# Revit family: Cabinet_Base-Cabinet_45-Degree-With-Overhead-Countertop_Moduline
name_source: partatom
category: Furniture
units: mm (PartAtom-declared; Revit-internal decimal feet)

## family parameters
Always vertical = Yes
Classification Number = 23.40.20.00
Cut with Voids When Loaded = No
Enable Cutting in Views = No
Render Appearance Source = Family Geometry
Room Calculation Point = No
Shared = No
Work Plane-Based = No

## types (4) — shared parameters
Depth = 24 "
Door Clearance = 15 "
Keynote = 12 35 00
Manufacturer = Moduline Aluminum Cabinets
Model = Pro II 45 Degree Base With Ovehead Cabinet
Product Page URL = https://www.arcat.com
URL = https://modulinecabinets.com
Width = 30 "
zero-valued in all types: Default Elevation

## per-type parameters (varying)
| type | Description | Height | Overhead Height |
| 36"H x 24"D x 30"W With 24"H Overhead | Modular 45 Degree Base With Ovehead Cabinet, Double Door, 36" Height x 24" Depth x 30" Width With 24"H Overhead | 35.875 " | 24 " |
| 32"H x 24"D x 30"W With 18"H Overhead | Modular 45 Degree Base With Ovehead Cabinet, Double Door, 32" Height x 24" Depth x 30" Width With 18"H Overhead | 31.875 " | 18 " |
| 36"H x 24"D x 30"W With 18"H Overhead | Modular 45 Degree Base With Ovehead Cabinet, Double Door, 36" Height x 24" Depth x 30" Width With 18"H Overhead | 35.875 " | 18 " |
| 32"H x 24"D x 30"W With 24"H Overhead | Modular 45 Degree Base With Ovehead Cabinet, Double Door, 32" Height x 24" Depth x 30" Width With 24"H Overhead | 31.875 " | 24 " |

## geometry (parser evidence)
native form markers: Sweep x16
no freeform markers — native parametric forms only
